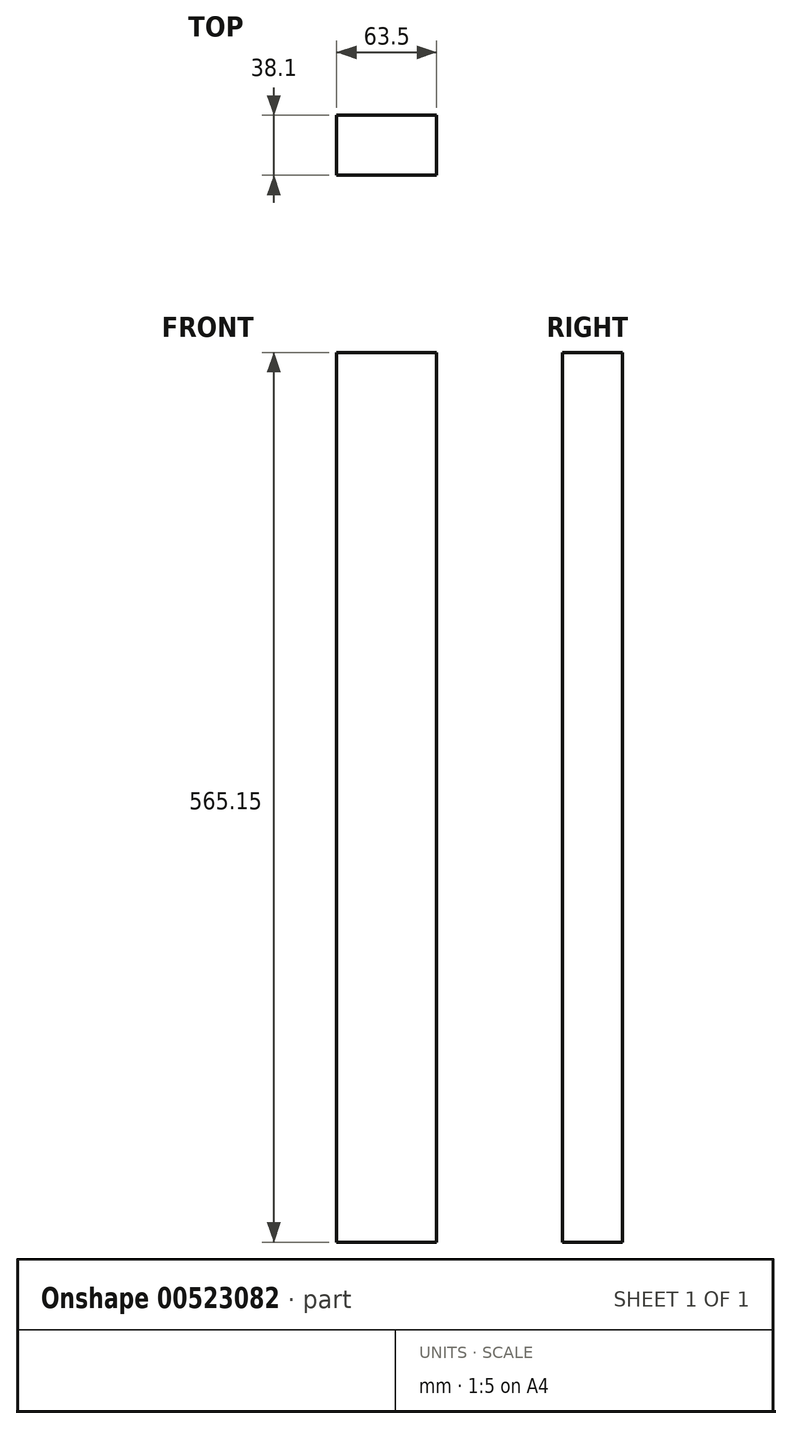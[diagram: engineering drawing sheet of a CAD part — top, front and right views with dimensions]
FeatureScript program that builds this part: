
annotation { "Feature Type Name" : "Feature", "Feature Type Description" : "" }
export const myFeature = defineFeature(function(context is Context, id is Id, definition is map)
    precondition{}
    {
        {
            var Q0;
            Q0=qCreatedBy(makeId("Top.planeOp"),FACE);
            var sketch = newSketch(context, id + "F0", { "sketchPlane" : qUnion([Q0])});
            skLineSegment(sketch, "E0.bottom", {"start": v(0, 0) * mm, "end": v(63.5, 0) * mm});
            skLineSegment(sketch, "E0.top", {"start": v(0, 38.1) * mm, "end": v(63.5, 38.1) * mm});
            skLineSegment(sketch, "E0.left", {"start": v(0, 0) * mm, "end": v(0, 38.1) * mm});
            skLineSegment(sketch, "E0.right", {"start": v(63.5, 0) * mm, "end": v(63.5, 38.1) * mm});
            skSolve(sketch);
        }
        {
            var Q0;
            Q0 = qSketchRegion(id + "F0", true);
            extrude(context, id + "F1", {"entities" : qUnion([Q0]), "depth" : 565.15 * mm, "offsetDistance" : 25.4 * mm});
        }
    });
